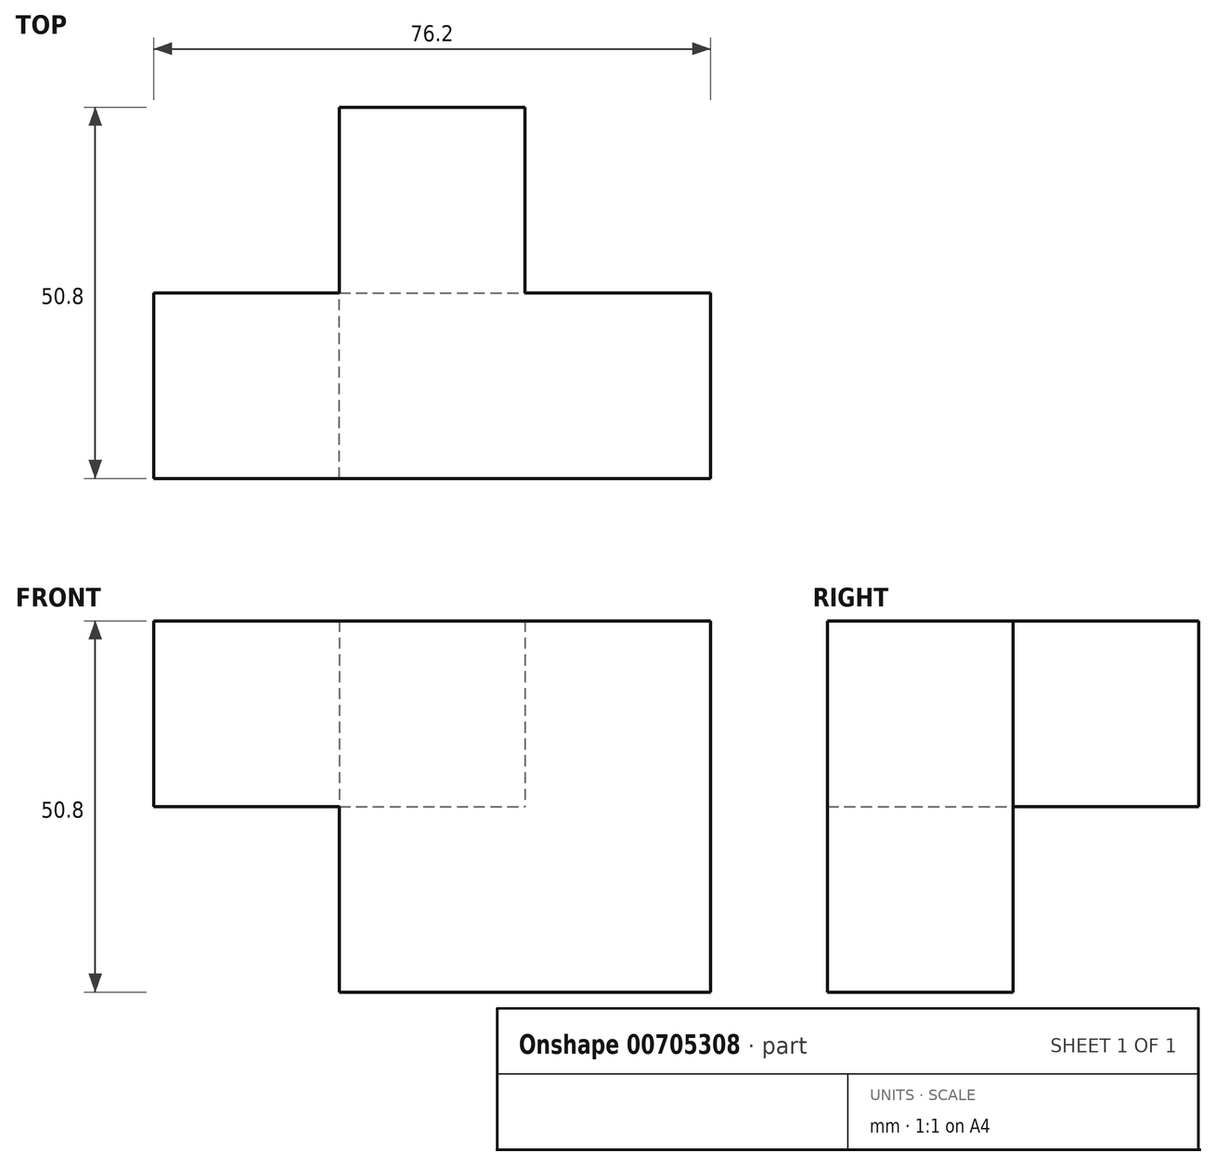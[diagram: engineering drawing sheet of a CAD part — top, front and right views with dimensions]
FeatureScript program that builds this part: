
annotation { "Feature Type Name" : "Feature", "Feature Type Description" : "" }
export const myFeature = defineFeature(function(context is Context, id is Id, definition is map)
    precondition{}
    {
        {
            var Q0;
            Q0=qCreatedBy(makeId("Front.planeOp"),FACE);
            var sketch = newSketch(context, id + "F0", { "sketchPlane" : qUnion([Q0])});
            skLineSegment(sketch, "E0.bottom", {"start": v(0, 0) * mm, "end": v(25.4, 0) * mm});
            skLineSegment(sketch, "E0.top", {"start": v(0, 25.4) * mm, "end": v(25.4, 25.4) * mm});
            skLineSegment(sketch, "E0.left", {"start": v(0, 0) * mm, "end": v(0, 25.4) * mm});
            skLineSegment(sketch, "E0.right", {"start": v(25.4, 0) * mm, "end": v(25.4, 25.4) * mm});
            skLineSegment(sketch, "E1.bottom", {"start": v(25.4, 25.4) * mm, "end": v(50.8, 25.4) * mm});
            skLineSegment(sketch, "E1.top", {"start": v(25.4, 0) * mm, "end": v(50.8, 0) * mm});
            skLineSegment(sketch, "E1.left", {"start": v(25.4, 25.4) * mm, "end": v(25.4, 0) * mm});
            skLineSegment(sketch, "E1.right", {"start": v(50.8, 25.4) * mm, "end": v(50.8, 0) * mm});
            skLineSegment(sketch, "E2.bottom", {"start": v(50.8, 0) * mm, "end": v(25.4, 0) * mm});
            skLineSegment(sketch, "E2.top", {"start": v(50.8, -25.4) * mm, "end": v(25.4, -25.4) * mm});
            skLineSegment(sketch, "E2.left", {"start": v(50.8, 0) * mm, "end": v(50.8, -25.4) * mm});
            skLineSegment(sketch, "E2.right", {"start": v(25.4, 0) * mm, "end": v(25.4, -25.4) * mm});
            skLineSegment(sketch, "E3.top", {"start": v(0, -25.4) * mm, "end": v(25.4, -25.4) * mm});
            skLineSegment(sketch, "E3.left", {"start": v(0, 0) * mm, "end": v(0, -25.4) * mm});
            skLineSegment(sketch, "E4.bottom", {"start": v(0, 25.4) * mm, "end": v(-25.4, 25.4) * mm});
            skLineSegment(sketch, "E4.top", {"start": v(0, 0) * mm, "end": v(-25.4, 0) * mm});
            skLineSegment(sketch, "E4.left", {"start": v(0, 25.4) * mm, "end": v(0, 0) * mm});
            skLineSegment(sketch, "E4.right", {"start": v(-25.4, 25.4) * mm, "end": v(-25.4, 0) * mm});
            skSolve(sketch);
        }
        {
            var Q0;
            Q0 = qSketchRegion(id + "F0", true);
            extrude(context, id + "F1", {"entities" : qUnion([Q0]), "depth" : 25.4 * mm, "offsetDistance" : 25.4 * mm});
        }
        {
            var Q0;
            Q0=qCreatedBy(makeId("Top.planeOp"),FACE);
            var sketch = newSketch(context, id + "F2", { "sketchPlane" : qUnion([Q0])});
            skLineSegment(sketch, "E5.bottom", {"start": v(0, 0) * mm, "end": v(25.4, 0) * mm});
            skLineSegment(sketch, "E5.top", {"start": v(0, 25.4) * mm, "end": v(25.4, 25.4) * mm});
            skLineSegment(sketch, "E5.left", {"start": v(0, 0) * mm, "end": v(0, 25.4) * mm});
            skLineSegment(sketch, "E5.right", {"start": v(25.4, 0) * mm, "end": v(25.4, 25.4) * mm});
            skSolve(sketch);
        }
        {
            var Q0;
            Q0=makeQuery(id+"F2.imprint","IMPRINT",FACE,{"disambiguationData":[TD([[makeQuery(id+"F2.imprint","IMPRINT",EDGE,{"derivedFrom":sQuery(id+"F2.wireOp",EDGE,"E5.bottom")}),1.0]])]});
            extrude(context, id + "F3", {"entities" : qUnion([Q0]), "operationType" : NewBodyOperationType.ADD, "depth" : 25.4 * mm, "offsetDistance" : 25.4 * mm});
        }
    });
